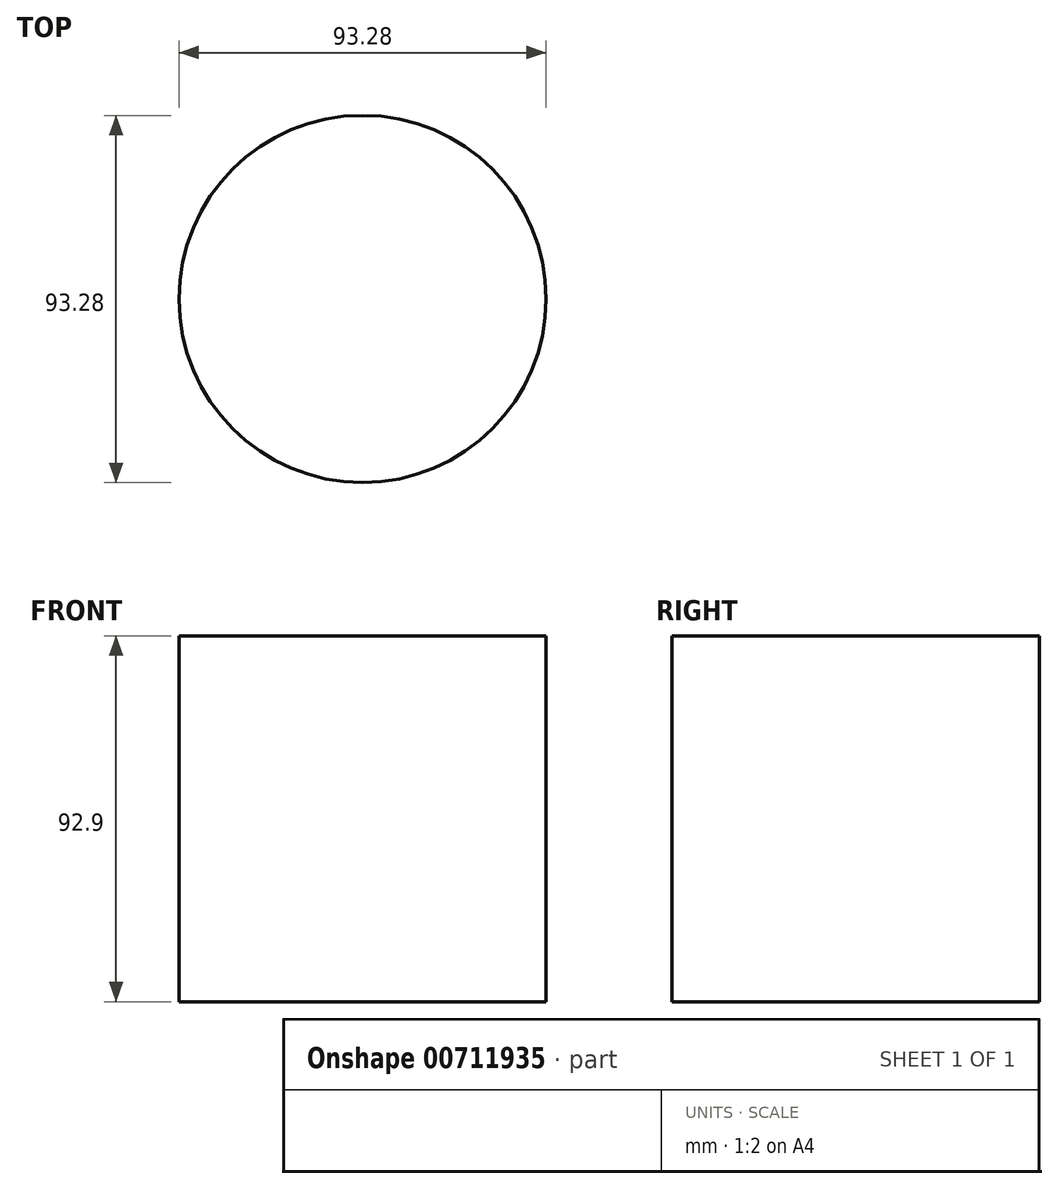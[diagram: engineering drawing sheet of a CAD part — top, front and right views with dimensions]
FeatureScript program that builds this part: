
annotation { "Feature Type Name" : "Feature", "Feature Type Description" : "" }
export const myFeature = defineFeature(function(context is Context, id is Id, definition is map)
    precondition{}
    {
        {
            var Q0;
            Q0=qCreatedBy(makeId("Top.planeOp"),FACE);
            var sketch = newSketch(context, id + "F0", { "sketchPlane" : qUnion([Q0])});
            skCircle(sketch, "E0", {"center": v(0, 0) * mm, "radius": 46.64 * mm});
            skSolve(sketch);
        }
        {
            var Q0;
            Q0=sQuery(id+"F0.wireOp",EDGE,"E0");
            extrude(context, id + "F1", {"bodyType" : ToolBodyType.SURFACE, "surfaceEntities" : qUnion([Q0]), "depth" : 92.9 * mm, "offsetDistance" : 25.4 * mm});
        }
    });
